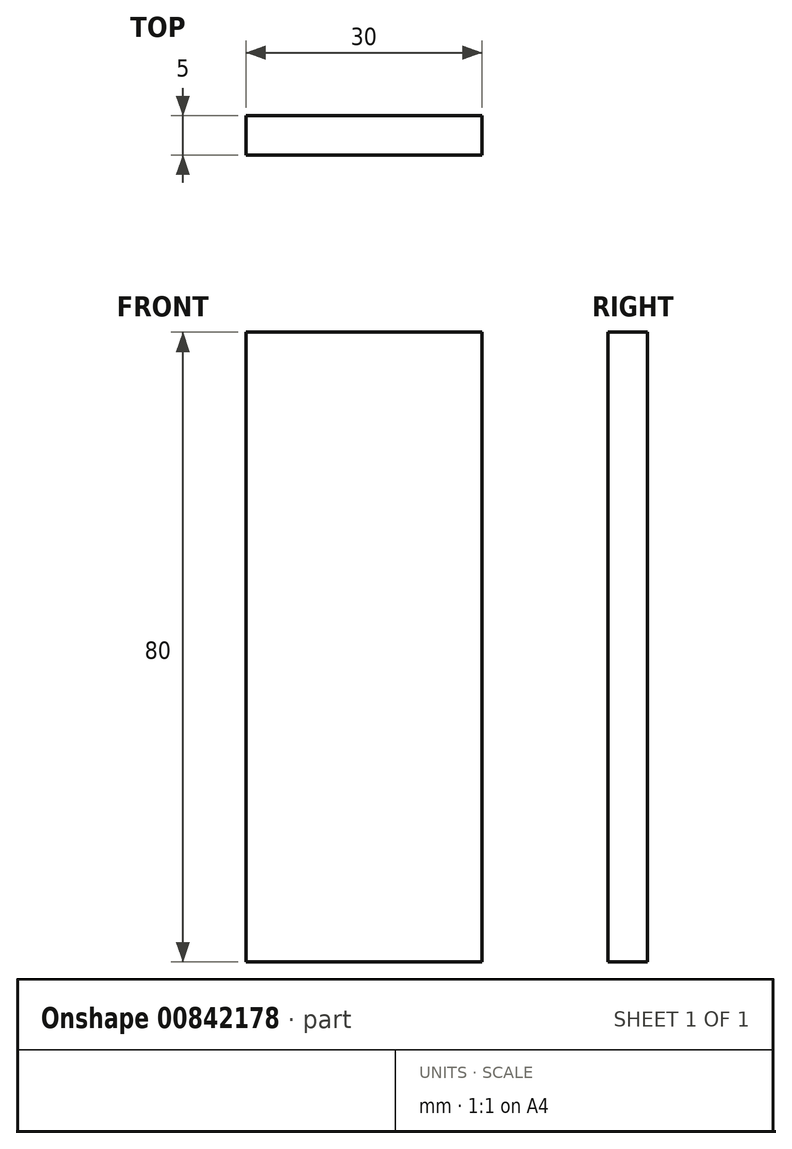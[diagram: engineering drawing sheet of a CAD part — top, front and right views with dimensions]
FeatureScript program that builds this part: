
annotation { "Feature Type Name" : "Feature", "Feature Type Description" : "" }
export const myFeature = defineFeature(function(context is Context, id is Id, definition is map)
    precondition{}
    {
        {
            var Q0;
            Q0=qCreatedBy(makeId("Front.planeOp"),FACE);
            var sketch = newSketch(context, id + "F0", { "sketchPlane" : qUnion([Q0])});
            skLineSegment(sketch, "E0.bottom", {"start": v(0, 0) * mm, "end": v(30, 0) * mm});
            skLineSegment(sketch, "E0.top", {"start": v(0, 80) * mm, "end": v(30, 80) * mm});
            skLineSegment(sketch, "E0.left", {"start": v(0, 0) * mm, "end": v(0, 80) * mm});
            skLineSegment(sketch, "E0.right", {"start": v(30, 0) * mm, "end": v(30, 80) * mm});
            skSolve(sketch);
        }
        {
            var Q0;
            Q0 = qSketchRegion(id + "F0", true);
            extrude(context, id + "F1", {"entities" : qUnion([Q0]), "depth" : 5 * mm, "offsetDistance" : 25 * mm});
        }
    });
